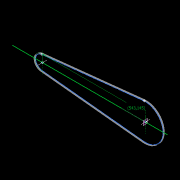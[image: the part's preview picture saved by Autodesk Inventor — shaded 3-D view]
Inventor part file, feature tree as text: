
AUTODESK INVENTOR PART (.ipt)
format: ipt  version: 2021 (Build 250183000, 183)  size: 131,072 bytes
history: native  units: mm
features: other x67, plane x3, pattern_linear x3, sketch x2, extrude x1
ambient origin geometry x8: Origin, YZ Plane, XZ Plane, XY Plane, X Axis, Y Axis, Z Axis, Center Point
bodies: Solid1 (feature_tree), Solid (feature_tree)
feature tree (76):
  other  "Work Axis1"
  other  "Work Axis2"
  plane  "Work Plane2"
  plane  "Work Plane3"
  other  "Path"
  other  "Section Plane"
  pattern_linear  "Strand Pattern"  Spacing1=3.66mm  [1 undecoded]
  other  "Work Point10"
  other  "Work Point11"
  other  "Work Point12"
  sketch  "Sketch5"  dims[d4=0.0mm d21=3.66mm d22=7.75mm d23=3.3mm d24=2.0mm d28=10.0mm d30=13.92mm d31=9.91mm d32=10.2mm d33=0.0mm d34=0.0mm d35=0.0mm d36=0.0mm d37=0.0mm d38=3.875mm d39=10.0mm d40=0.0mm d42=543.145102mm d43=20.0mm d45=543.145102mm d46=0.0mm d47=580.0mm]
  pattern_linear  "Rectangular Pattern5"  Spacing1=7.75mm  [1 undecoded]
  plane  "Work Plane7"
  pattern_linear  "Rectangular Pattern6"  Spacing1=3.3mm  [1 undecoded]
  other  "Section Sketch"
  sketch  "Sketch4"  dims[d2=0.0mm]
  other  "Srf1"
  other  "Work Point13"
  other  "Work Point14"
  other  "Work Point15"
  other  "Work Point16"
  other  "Work Point17"
  other  "Work Point18"
  other  "Work Point19"
  other  "Work Point20"
  other  "Work Point21"
  other  "Work Point22"
  other  "Work Point23"
  other  "Work Point24"
  other  "Work Point25"
  other  "Work Point26"
  other  "Work Point27"
  other  "Work Point28"
  other  "Work Point29"
  other  "Work Point30"
  other  "Work Point31"
  other  "Work Point32"
  other  "Work Point33"
  other  "Work Point34"
  other  "Work Point35"
  other  "Work Point36"
  other  "Work Point37"
  other  "Work Point38"
  other  "Work Point39"
  other  "Work Point40"
  other  "Work Point41"
  other  "Work Point42"
  other  "Work Point43"
  other  "Work Point44"
  other  "Work Point45"
  other  "Work Point46"
  other  "Work Point47"
  other  "Work Point48"
  other  "Work Point49"
  other  "Work Point50"
  other  "Work Point51"
  other  "Work Point52"
  other  "Work Point53"
  other  "Work Point54"
  other  "Work Point55"
  other  "Work Point56"
  other  "Work Point57"
  other  "Work Point58"
  other  "Work Point59"
  other  "Work Point60"
  other  "Work Point61"
  other  "Work Point62"
  other  "Work Point63"
  other  "Work Point64"
  other  "Work Point65"
  other  "Work Point66"
  other  "Work Point67"
  other  "Work Point68"
  other  "Work Point69"
  other  "Work Point70"
  extrude  "ExtrusionSrf1"  Depth=543.145102mm
note: 3 required parameter values undecoded (feature->parameter linkage not recoverable at this tier; creation-order binding heuristic only, values carry confidence <= 0.55)
